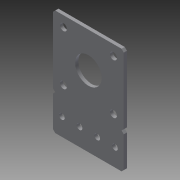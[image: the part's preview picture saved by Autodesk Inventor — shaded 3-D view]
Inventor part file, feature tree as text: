
AUTODESK INVENTOR PART (.ipt)
format: ipt  version: 2014 SP1 (Build 180222100, 222)  size: 154,624 bytes
history: native  units: in
note: dims shown in document units (in); Inventor stores cm internally (conversion verified against a paired STEP export)
features: other x1, extrude x1, imported_body x1, sketch x1
ambient origin geometry x8: Origin, YZ Plane, XZ Plane, XY Plane, X Axis, Y Axis, Z Axis, Center Point
bodies: Body1 (feature_tree)
feature tree (4):
  other  "Cut-Extrude1"
  extrude  "Extrusion2"  [1 undecoded]
  imported_body  "Base1"
  sketch  "Sketch2"  dims[d3=1.0in d4=0.0in]
note: 1 required parameter value undecoded (feature->parameter linkage not recoverable at this tier; creation-order binding heuristic only, values carry confidence <= 0.55)
